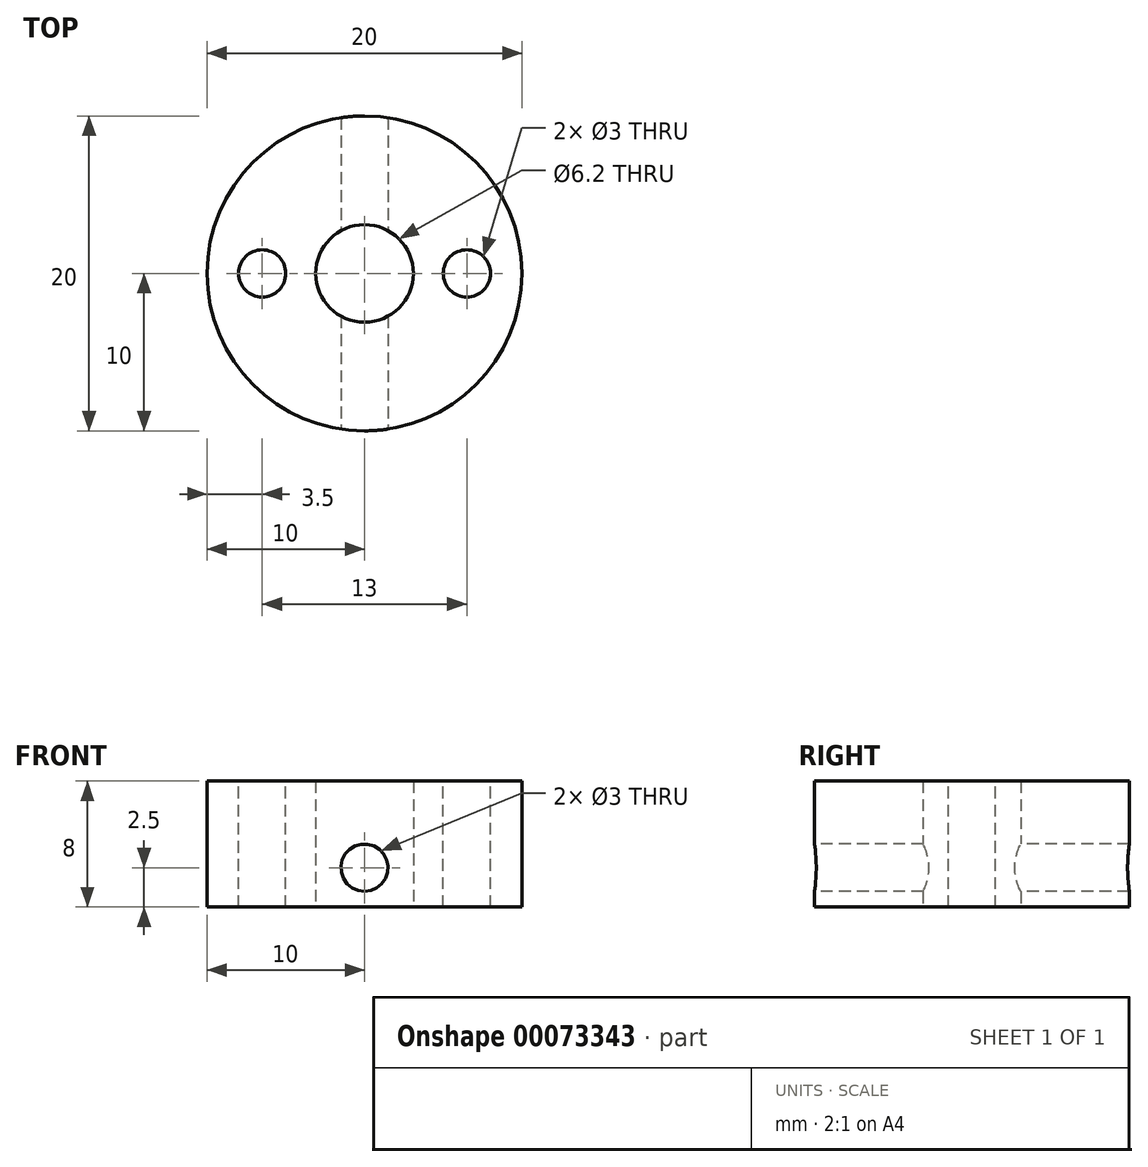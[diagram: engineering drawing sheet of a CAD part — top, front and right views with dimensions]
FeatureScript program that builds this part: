
annotation { "Feature Type Name" : "Feature", "Feature Type Description" : "" }
export const myFeature = defineFeature(function(context is Context, id is Id, definition is map)
    precondition{}
    {
        {
            var Q0;
            Q0=qCreatedBy(makeId("Top.planeOp"),FACE);
            var sketch = newSketch(context, id + "F0", { "sketchPlane" : qUnion([Q0])});
            skCircle(sketch, "E0", {"center": v(0, 0) * mm, "radius": 10 * mm});
            skCircle(sketch, "E1", {"center": v(0, 0) * mm, "radius": 3.1 * mm});
            skSolve(sketch);
        }
        {
            var Q0;
            Q0=makeQuery(id+"F0.imprint","IMPRINT",FACE,{"disambiguationData":[TD([[makeQuery(id+"F0.imprint","IMPRINT",EDGE,{"derivedFrom":sQuery(id+"F0.wireOp",EDGE,"E0")}),1.0]])]});
            extrude(context, id + "F1", {"entities" : qUnion([Q0]), "depth" : 5 * mm, "offsetDistance" : 25 * mm, "symmetric" : true});
        }
        {
            var Q0;
            Q0=makeQuery(id+"F1.opExtrude","CAP_FACE",FACE,{"disambiguationData":[OSD([sQuery(id+"F0.wireOp",EDGE,"E0"),sQuery(id+"F0.wireOp",EDGE,"E1")])],"isStart":false});
            var sketch = newSketch(context, id + "F2", { "sketchPlane" : qUnion([Q0])});
            skCircle(sketch, "E2", {"center": v(0, 0) * mm, "radius": 6.5 * mm});
            skPoint(sketch, "E3", {"position": v(-6.5, 0) * mm});
            skPoint(sketch, "E4", {"position": v(6.5, 0) * mm});
            skSolve(sketch);
        }
        {
            var Q0;
            Q0=sQuery(id+"F2.wireOp",VERTEX,"E3");
            var Q1;
            Q1=sQuery(id+"F2.wireOp",VERTEX,"E4");
            var Q2;
            Q2=makeQuery(id+"F1.opExtrude","SWEPT_BODY",BODY,{"disambiguationData":[OSD([sQuery(id+"F0.wireOp",EDGE,"E0"),sQuery(id+"F0.wireOp",EDGE,"E1")])]});
            hole(context, id + "F3", {"style" : HoleStyle.SIMPLE, "endStyle" : HoleEndStyle.THROUGH, "holeDiameter" : 3 * mm, "majorDiameter" : 5 * mm, "tappedDepth" : 12 * mm, "tapClearance" : 3, "locations" : qUnion([Q0, Q1]), "scope" : qUnion([Q2])});
        }
        {
            var Q0;
            Q0=qCreatedBy(makeId("Front.planeOp"),FACE);
            var sketch = newSketch(context, id + "F4", { "sketchPlane" : qUnion([Q0])});
            skCircle(sketch, "E5", {"center": v(0, 0) * mm, "radius": 1.5 * mm});
            skSolve(sketch);
        }
        {
            var Q0;
            Q0=makeQuery(id+"F4.imprint","IMPRINT",FACE,{"disambiguationData":[TD([[makeQuery(id+"F4.imprint","IMPRINT",EDGE,{"derivedFrom":sQuery(id+"F4.wireOp",EDGE,"E5")}),1.0]])]});
            extrude(context, id + "F5", {"entities" : qUnion([Q0]), "operationType" : NewBodyOperationType.REMOVE, "oppositeDirection" : true, "depth" : 25 * mm, "offsetDistance" : 25 * mm, "symmetric" : true});
        }
        {
            var Q0;
            Q0=makeQuery(id+"F1.opExtrude","CAP_FACE",FACE,{"disambiguationData":[OSD([sQuery(id+"F0.wireOp",EDGE,"E0"),sQuery(id+"F0.wireOp",EDGE,"E1")])],"isStart":false});
            extrude(context, id + "F6", {"entities" : qUnion([Q0]), "operationType" : NewBodyOperationType.ADD, "depth" : 3 * mm, "offsetDistance" : 25 * mm});
        }
    });
